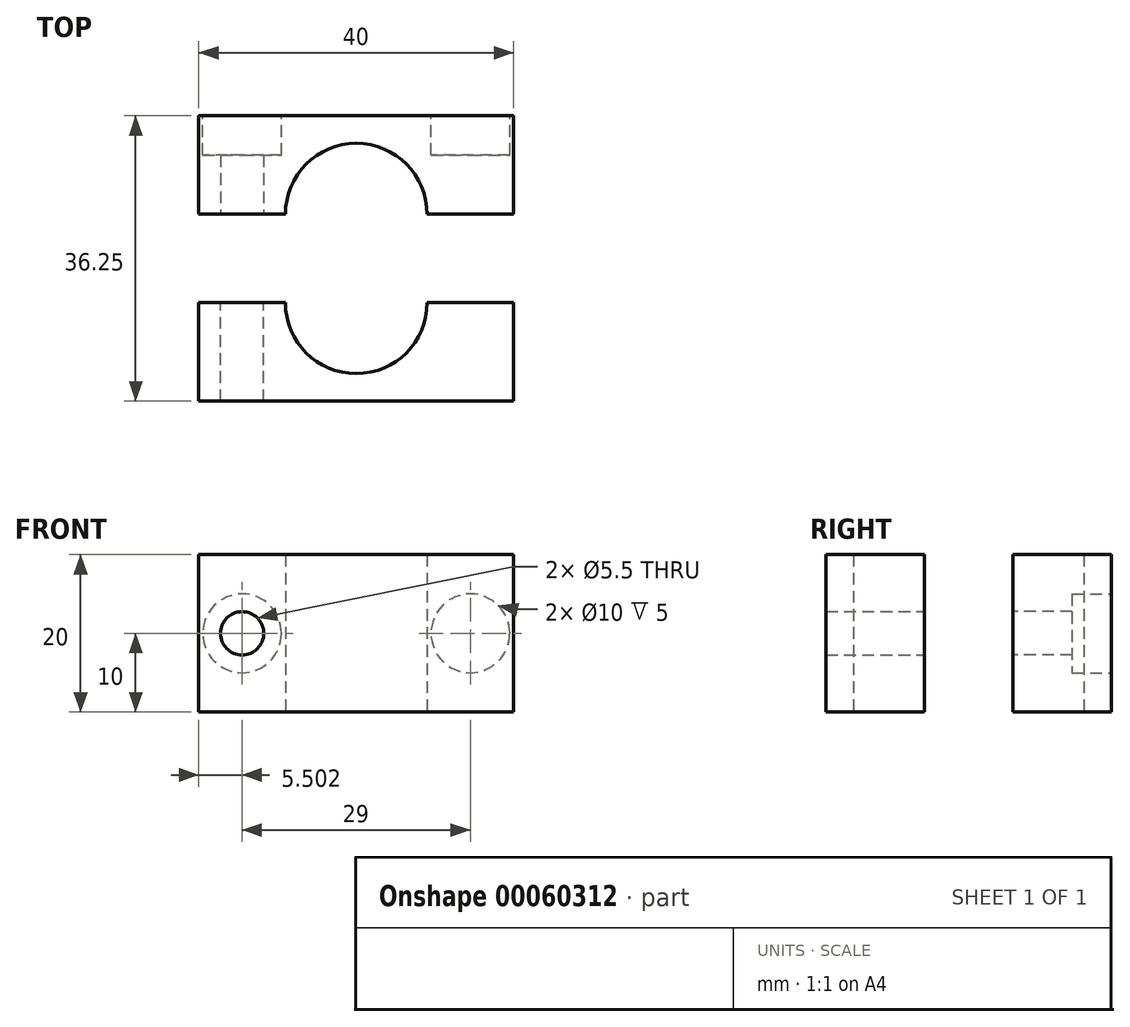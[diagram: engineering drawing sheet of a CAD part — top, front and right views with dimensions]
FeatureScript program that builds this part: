
annotation { "Feature Type Name" : "Feature", "Feature Type Description" : "" }
export const myFeature = defineFeature(function(context is Context, id is Id, definition is map)
    precondition{}
    {
        {
            var Q0;
            Q0=qCreatedBy(makeId("Top.planeOp"),FACE);
            var sketch = newSketch(context, id + "F0", { "sketchPlane" : qUnion([Q0])});
            skLineSegment(sketch, "E0.bottom", {"start": v(-34.4, 4.99) * mm, "end": v(5.6, 4.99) * mm});
            skLineSegment(sketch, "E0.top", {"start": v(-34.4, -7.51) * mm, "end": v(5.6, -7.51) * mm});
            skLineSegment(sketch, "E0.left", {"start": v(-34.4, 4.99) * mm, "end": v(-34.4, -7.51) * mm});
            skLineSegment(sketch, "E0.right", {"start": v(5.6, 4.99) * mm, "end": v(5.6, -7.51) * mm});
            skLineSegment(sketch, "E1.bottom", {"start": v(-34.4, 16.24) * mm, "end": v(5.6, 16.24) * mm});
            skLineSegment(sketch, "E1.top", {"start": v(-34.4, 28.74) * mm, "end": v(5.6, 28.74) * mm});
            skLineSegment(sketch, "E1.left", {"start": v(-34.4, 16.24) * mm, "end": v(-34.4, 28.74) * mm});
            skLineSegment(sketch, "E1.right", {"start": v(5.6, 16.24) * mm, "end": v(5.6, 28.74) * mm});
            skArc(sketch, "E2", {"start": v(-5.4, 16.24) * mm, "mid": v(-14.4, 25.24) * mm, "end": v(-23.4, 16.24) * mm});
            skArc(sketch, "E3", {"start": v(-23.4, 4.99) * mm, "mid": v(-14.4, -4.01) * mm, "end": v(-5.4, 4.99) * mm});
            skSolve(sketch);
        }
        {
            var Q0;
            Q0=makeQuery(id+"F0.imprint","IMPRINT",FACE,{"disambiguationData":[TD([[makeQuery(id+"F0.imprint","IMPRINT",EDGE,{"derivedFrom":sQuery(id+"F0.wireOp",EDGE,"E1.top")}),-1.0]])]});
            var Q1;
            Q1=makeQuery(id+"F0.imprint","IMPRINT",FACE,{"disambiguationData":[TD([[makeQuery(id+"F0.imprint","IMPRINT",EDGE,{"derivedFrom":sQuery(id+"F0.wireOp",EDGE,"E0.top")}),1.0]])]});
            extrude(context, id + "F1", {"entities" : qUnion([Q0, Q1]), "depth" : 20 * mm});
        }
        {
            var Q0;
            {var subQ0=sQuery(id+"F0.wireOp",EDGE,"E0.bottom");Q0=makeQuery(id+"F1.opExtrude","SWEPT_FACE",FACE,{"disambiguationData":[OSD([subQ0]),TDD([makeQuery(id+"F0.imprint","IMPRINT",EDGE,{"disambiguationData":[TD([[makeQuery(id+"F0.imprint","INTERSECT",VERTEX,{"derivedFrom":[subQ0,sQuery(id+"F0.wireOp",EDGE,"E0.left")]}),-1.0]])],"derivedFrom":subQ0})])]});}
            var sketch = newSketch(context, id + "F2", { "sketchPlane" : qUnion([Q0])});
            skLineSegment(sketch, "E4", {"start": v(34.4, 10) * mm, "end": v(0, 10) * mm, "construction": true});
            skLineSegment(sketch, "E5", {"start": v(28.9, 20) * mm, "end": v(28.9, 0) * mm, "construction": true});
            skLineSegment(sketch, "E6", {"start": v(17.2, 10) * mm, "end": v(17.2, 20.05) * mm, "construction": true});
            skCircle(sketch, "E7", {"center": v(28.9, 10) * mm, "radius": 2.75 * mm});
            skCircle(sketch, "E8.MirrorC", {"center": v(-0.1, 10) * mm, "radius": 2.75 * mm});
            skSolve(sketch);
        }
        {
            var Q0;
            Q0=makeQuery(id+"F2.imprint","IMPRINT",FACE,{"disambiguationData":[TD([[makeQuery(id+"F2.imprint","IMPRINT",EDGE,{"derivedFrom":sQuery(id+"F2.wireOp",EDGE,"E8.MirrorC")}),-1.0]])]});
            var Q1;
            Q1=makeQuery(id+"F2.imprint","IMPRINT",FACE,{"disambiguationData":[TD([[makeQuery(id+"F2.imprint","IMPRINT",EDGE,{"derivedFrom":sQuery(id+"F2.wireOp",EDGE,"E7")}),1.0]])]});
            extrude(context, id + "F3", {"entities" : qUnion([Q0, Q1]), "operationType" : NewBodyOperationType.REMOVE, "oppositeDirection" : true, "depth" : 25 * mm});
        }
        {
            var Q0;
            {var subQ0=sQuery(id+"F0.wireOp",EDGE,"E1.bottom");Q0=makeQuery(id+"F1.opExtrude","SWEPT_FACE",FACE,{"disambiguationData":[OSD([subQ0]),TDD([makeQuery(id+"F0.imprint","IMPRINT",EDGE,{"disambiguationData":[TD([[makeQuery(id+"F0.imprint","INTERSECT",VERTEX,{"derivedFrom":[subQ0,sQuery(id+"F0.wireOp",EDGE,"E1.left")]}),-1.0]])],"derivedFrom":subQ0})])]});}
            var sketch = newSketch(context, id + "F4", { "sketchPlane" : qUnion([Q0])});
            skLineSegment(sketch, "E9", {"start": v(-34.4, 10) * mm, "end": v(0.82, 10) * mm, "construction": true});
            skLineSegment(sketch, "E10", {"start": v(-28.9, 20) * mm, "end": v(-28.9, 0) * mm, "construction": true});
            skCircle(sketch, "E11", {"center": v(-28.9, 10) * mm, "radius": 2.75 * mm});
            skCircle(sketch, "E12.MirrorC", {"center": v(0.1, 10) * mm, "radius": 2.75 * mm});
            skSolve(sketch);
        }
        {
            var Q0;
            Q0=makeQuery(id+"F4.imprint","IMPRINT",FACE,{"disambiguationData":[TD([[makeQuery(id+"F4.imprint","IMPRINT",EDGE,{"derivedFrom":sQuery(id+"F4.wireOp",EDGE,"E11")}),1.0]])]});
            var Q1;
            Q1=makeQuery(id+"F4.imprint","IMPRINT",FACE,{"disambiguationData":[TD([[makeQuery(id+"F4.imprint","IMPRINT",EDGE,{"derivedFrom":sQuery(id+"F4.wireOp",EDGE,"E12.MirrorC")}),-1.0]])]});
            extrude(context, id + "F5", {"entities" : qUnion([Q0, Q1]), "operationType" : NewBodyOperationType.REMOVE, "oppositeDirection" : true, "depth" : 12.5 * mm});
        }
        {
            var Q0;
            Q0=makeQuery(id+"F1.opExtrude","SWEPT_FACE",FACE,{"disambiguationData":[OSD([sQuery(id+"F0.wireOp",EDGE,"E1.top")])]});
            var sketch = newSketch(context, id + "F6", { "sketchPlane" : qUnion([Q0])});
            skCircle(sketch, "E13", {"center": v(-0.1, 10) * mm, "radius": 5 * mm});
            skCircle(sketch, "E14", {"center": v(28.9, 10) * mm, "radius": 5 * mm});
            skSolve(sketch);
        }
        {
            var Q0;
            Q0 = qSketchRegion(id + "F6", true);
            extrude(context, id + "F7", {"entities" : qUnion([Q0]), "operationType" : NewBodyOperationType.REMOVE, "oppositeDirection" : true, "depth" : 5 * mm});
        }
    });
